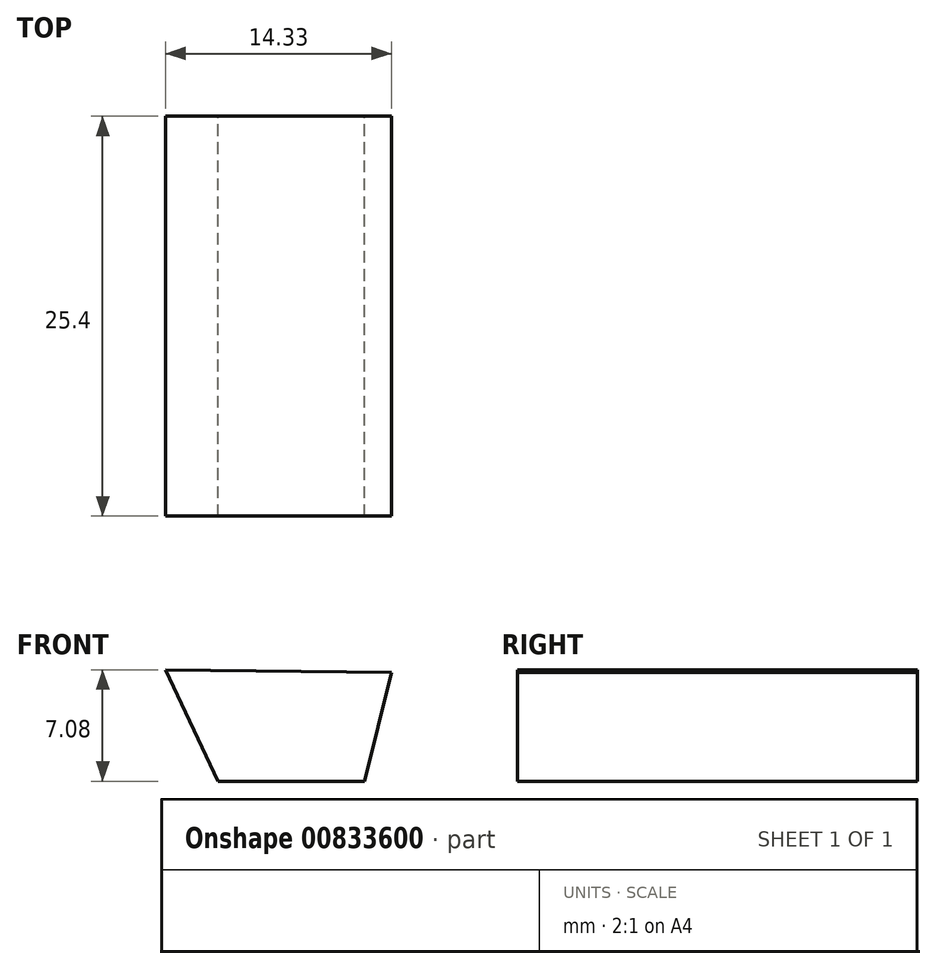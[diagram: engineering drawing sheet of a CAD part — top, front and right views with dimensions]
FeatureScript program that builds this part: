
annotation { "Feature Type Name" : "Feature", "Feature Type Description" : "" }
export const myFeature = defineFeature(function(context is Context, id is Id, definition is map)
    precondition{}
    {
        {
            var Q0;
            Q0=qCreatedBy(makeId("Front.planeOp"),FACE);
            var sketch = newSketch(context, id + "F0", { "sketchPlane" : qUnion([Q0])});
            skLineSegment(sketch, "E0", {"start": v(-6.42, -1.18) * mm, "end": v(2.88, -1.18) * mm});
            skLineSegment(sketch, "E1", {"start": v(2.88, -1.18) * mm, "end": v(4.57, 5.73) * mm});
            skLineSegment(sketch, "E2", {"start": v(4.57, 5.73) * mm, "end": v(-9.76, 5.9) * mm});
            skLineSegment(sketch, "E3", {"start": v(-9.76, 5.9) * mm, "end": v(-6.42, -1.18) * mm});
            skSolve(sketch);
        }
        {
            var Q0;
            Q0 = qSketchRegion(id + "F0", true);
            extrude(context, id + "F1", {"entities" : qUnion([Q0]), "depth" : 25.4 * mm, "offsetDistance" : 25.4 * mm});
        }
    });
